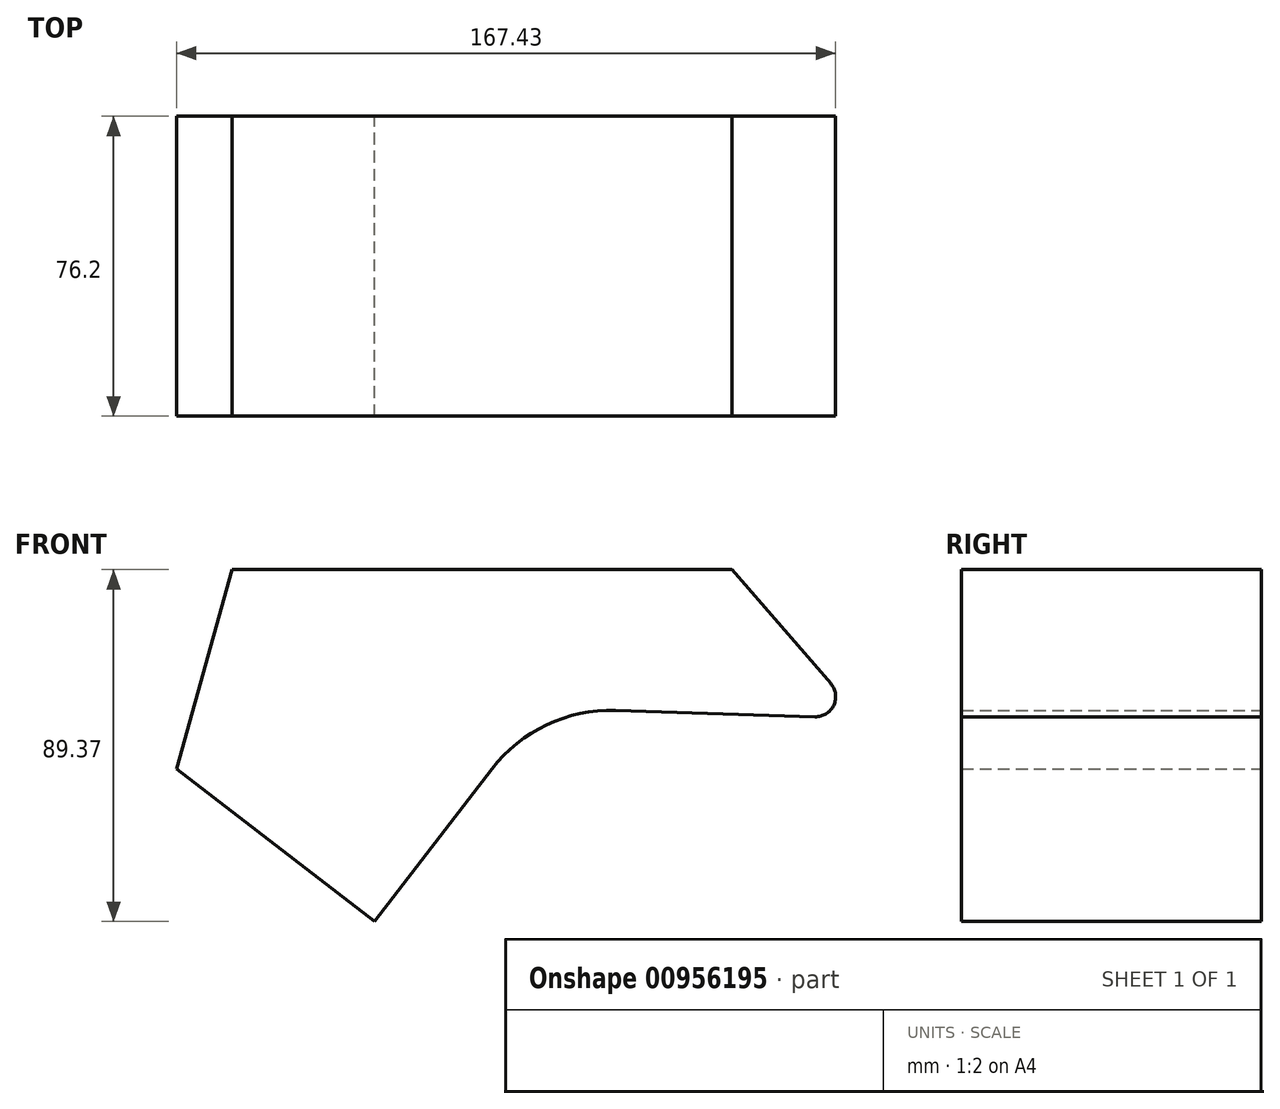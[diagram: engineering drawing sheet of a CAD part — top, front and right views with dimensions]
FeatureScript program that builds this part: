
annotation { "Feature Type Name" : "Feature", "Feature Type Description" : "" }
export const myFeature = defineFeature(function(context is Context, id is Id, definition is map)
    precondition{}
    {
        {
            var Q0;
            Q0=qCreatedBy(makeId("Front.planeOp"),FACE);
            var sketch = newSketch(context, id + "F0", { "sketchPlane" : qUnion([Q0])});
            skLineSegment(sketch, "E0", {"start": v(127, 0) * mm, "end": v(0, 0) * mm});
            skLineSegment(sketch, "E1", {"start": v(0, 0) * mm, "end": v(-14.1, -50.66) * mm});
            skLineSegment(sketch, "E2", {"start": v(-14.1, -50.66) * mm, "end": v(-14.1, -50.66) * mm});
            skLineSegment(sketch, "E3", {"start": v(36.25, -89.37) * mm, "end": v(-14.1, -50.66) * mm});
            skLineSegment(sketch, "E4", {"start": v(36.25, -89.37) * mm, "end": v(66.01, -50.66) * mm});
            skLineSegment(sketch, "E5", {"start": v(148.1, -37.39) * mm, "end": v(97.4, -35.8) * mm});
            skLineSegment(sketch, "E6", {"start": v(127, 0) * mm, "end": v(152.1, -28.99) * mm});
            skPoint(sketch, "E7.visualSharp", {"position": v(159.69, -37.75) * mm});
            skArc(sketch, "E7.filletArc", {"start": v(148.1, -37.39) * mm, "mid": v(152.84, -34.5) * mm, "end": v(152.1, -28.99) * mm});
            skPoint(sketch, "E8.visualSharp", {"position": v(77.9, -35.19) * mm});
            skArc(sketch, "E8.filletArc", {"start": v(97.4, -35.8) * mm, "mid": v(79.92, -39.44) * mm, "end": v(66.01, -50.66) * mm});
            skSolve(sketch);
        }
        {
            var Q0;
            Q0=makeQuery(id+"F0.imprint","IMPRINT",FACE,{"disambiguationData":[TD([[makeQuery(id+"F0.imprint","IMPRINT",EDGE,{"derivedFrom":sQuery(id+"F0.wireOp",EDGE,"E0")}),1.0]])]});
            extrude(context, id + "F1", {"entities" : qUnion([Q0]), "depth" : 76.2 * mm, "offsetDistance" : 25.4 * mm});
        }
    });
